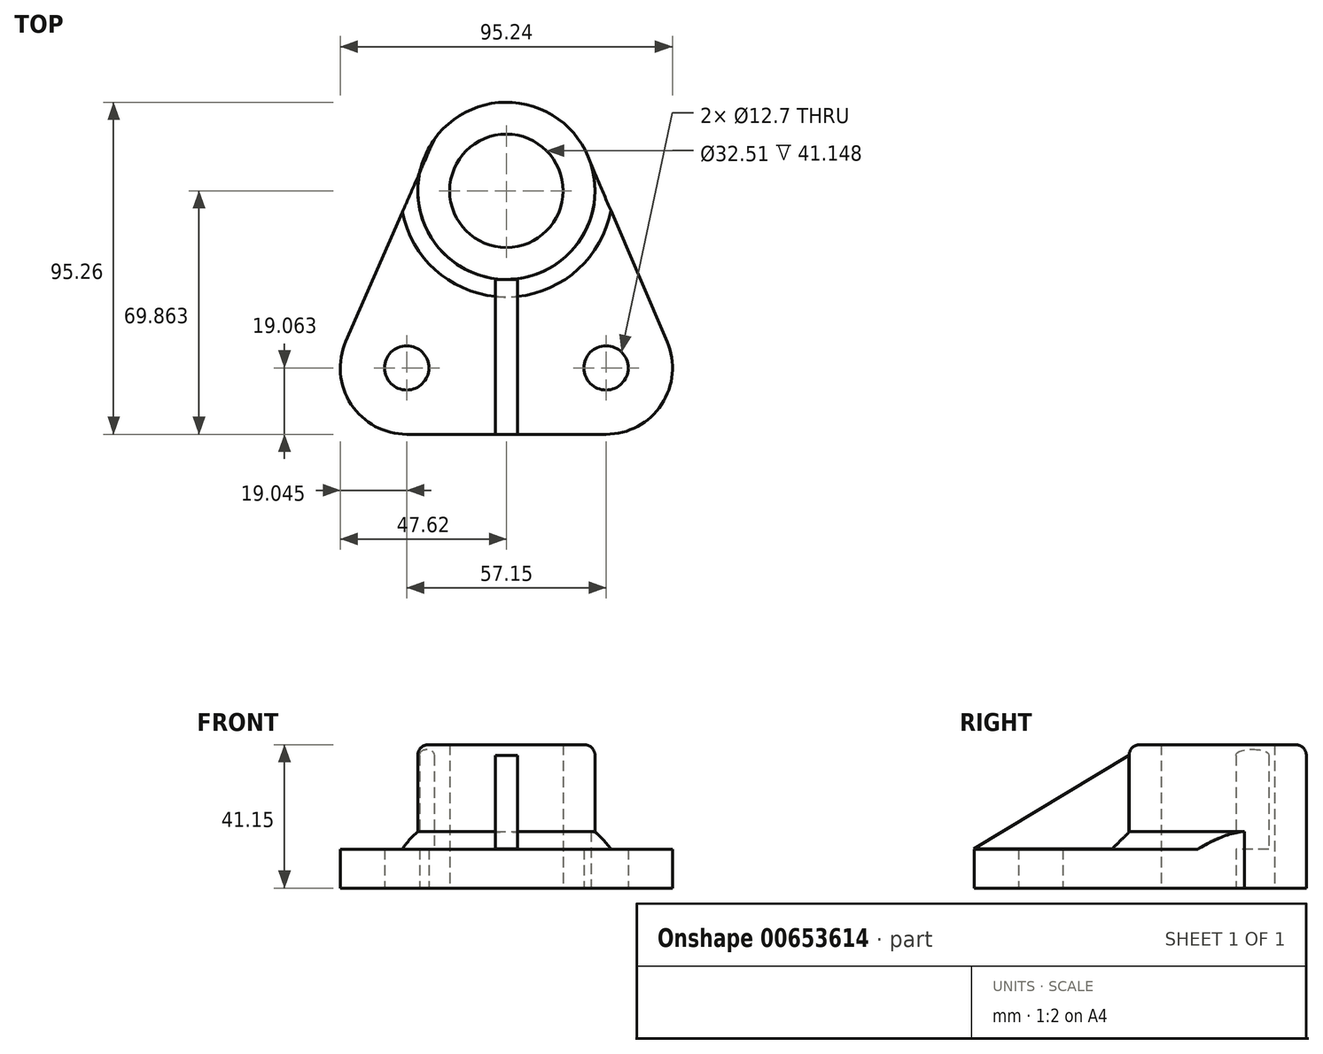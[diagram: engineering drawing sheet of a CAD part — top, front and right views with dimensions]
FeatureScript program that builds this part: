
annotation { "Feature Type Name" : "Feature", "Feature Type Description" : "" }
export const myFeature = defineFeature(function(context is Context, id is Id, definition is map)
    precondition{}
    {
        {
            var Q0;
            Q0=qCreatedBy(makeId("Top.planeOp"),FACE);
            var sketch = newSketch(context, id + "F0", { "sketchPlane" : qUnion([Q0])});
            skCircle(sketch, "E0", {"center": v(0, 7.28) * mm, "radius": 25.4 * mm});
            skCircle(sketch, "E1", {"center": v(0, 7.28) * mm, "radius": 16.26 * mm});
            skCircle(sketch, "E2", {"center": v(-28.57, -43.52) * mm, "radius": 6.35 * mm});
            skCircle(sketch, "E3", {"center": v(28.58, -43.52) * mm, "radius": 6.35 * mm});
            skArc(sketch, "E4", {"start": v(-46.03, -35.88) * mm, "mid": v(-44.52, -53.95) * mm, "end": v(-28.57, -62.57) * mm});
            skArc(sketch, "E5", {"start": v(28.58, -62.57) * mm, "mid": v(44.48, -54) * mm, "end": v(46.08, -36) * mm});
            skLineSegment(sketch, "E6", {"start": v(-20.74, 21.95) * mm, "end": v(-46.03, -35.88) * mm});
            skLineSegment(sketch, "E7", {"start": v(24.21, 14.95) * mm, "end": v(46.08, -36) * mm});
            skLineSegment(sketch, "E8", {"start": v(-28.57, -62.57) * mm, "end": v(28.58, -62.57) * mm});
            skPoint(sketch, "E9.orphan", {"position": v(0, -43.52) * mm});
            skSolve(sketch);
        }
        {
            var Q0;
            Q0=makeQuery(id+"F0.imprint","IMPRINT",FACE,{"disambiguationData":[TD([[makeQuery(id+"F0.imprint","IMPRINT",EDGE,{"derivedFrom":sQuery(id+"F0.wireOp",EDGE,"E0")}),1.0]])]});
            extrude(context, id + "F1", {"entities" : qUnion([Q0]), "depth" : 41.15 * mm, "offsetDistance" : 25.4 * mm});
        }
        {
            var Q0;
            Q0=makeQuery(id+"F1.opExtrude","CAP_EDGE",EDGE,{"disambiguationData":[OSD([sQuery(id+"F0.wireOp",EDGE,"E0")])],"isStart":false});
            fillet(context, id + "F2", {"entities" : qUnion([Q0]), "radius" : 3.05 * mm, "tangentPropagation" : true, "allowEdgeOverflow" : false});
        }
        {
            var Q0;
            Q0 = qSketchRegion(id + "F0", true);
            extrude(context, id + "F3", {"entities" : qUnion([Q0]), "operationType" : NewBodyOperationType.ADD, "depth" : 11.18 * mm, "offsetDistance" : 25.4 * mm});
        }
        {
            var Q0;
            {var subQ0=sQuery(id+"F0.wireOp",EDGE,"E0");Q0=makeQuery(id+"F3.boolean.opBoolean","INTERSECT",EDGE,{"derivedFrom":[makeQuery(id+"F1.opExtrude","SWEPT_FACE",FACE,{"disambiguationData":[OSD([subQ0])]}),makeQuery(id+"F3.opExtrude","SWEPT_FACE",FACE,{"disambiguationData":[OSD([subQ0])]}),makeQuery(id+"F3.opExtrude","CAP_FACE",FACE,{"disambiguationData":[OSD([subQ0,sQuery(id+"F0.wireOp",EDGE,"E1"),sQuery(id+"F0.wireOp",EDGE,"E2"),sQuery(id+"F0.wireOp",EDGE,"E3"),sQuery(id+"F0.wireOp",EDGE,"E4"),sQuery(id+"F0.wireOp",EDGE,"E5"),sQuery(id+"F0.wireOp",EDGE,"E6"),sQuery(id+"F0.wireOp",EDGE,"E7"),sQuery(id+"F0.wireOp",EDGE,"E8")])],"isStart":false})]});}
            chamfer(context, id + "F4", {"entities" : qUnion([Q0]), "width" : 5.08 * mm, "tangentPropagation" : true});
        }
        {
            var Q0;
            Q0=qCreatedBy(makeId("Right.planeOp"),FACE);
            var sketch = newSketch(context, id + "F5", { "sketchPlane" : qUnion([Q0])});
            skLineSegment(sketch, "E10", {"start": v(-18.18, 38.05) * mm, "end": v(-18.18, 11.26) * mm});
            skLineSegment(sketch, "E11", {"start": v(-18.18, 11.26) * mm, "end": v(-62.58, 11.26) * mm});
            skLineSegment(sketch, "E12", {"start": v(-62.58, 11.26) * mm, "end": v(-18.18, 38.05) * mm});
            skSolve(sketch);
        }
        {
            var Q0;
            Q0=makeQuery(id+"F5.imprint","IMPRINT",FACE,{"disambiguationData":[TD([[makeQuery(id+"F5.imprint","IMPRINT",EDGE,{"derivedFrom":sQuery(id+"F5.wireOp",EDGE,"E10")}),-1.0]])]});
            extrude(context, id + "F6", {"entities" : qUnion([Q0]), "operationType" : NewBodyOperationType.ADD, "depth" : 3.17 * mm, "offsetDistance" : 25.4 * mm, "hasSecondDirection" : true, "secondDirectionOppositeDirection" : true, "secondDirectionDepth" : 3.17 * mm});
        }
    });
